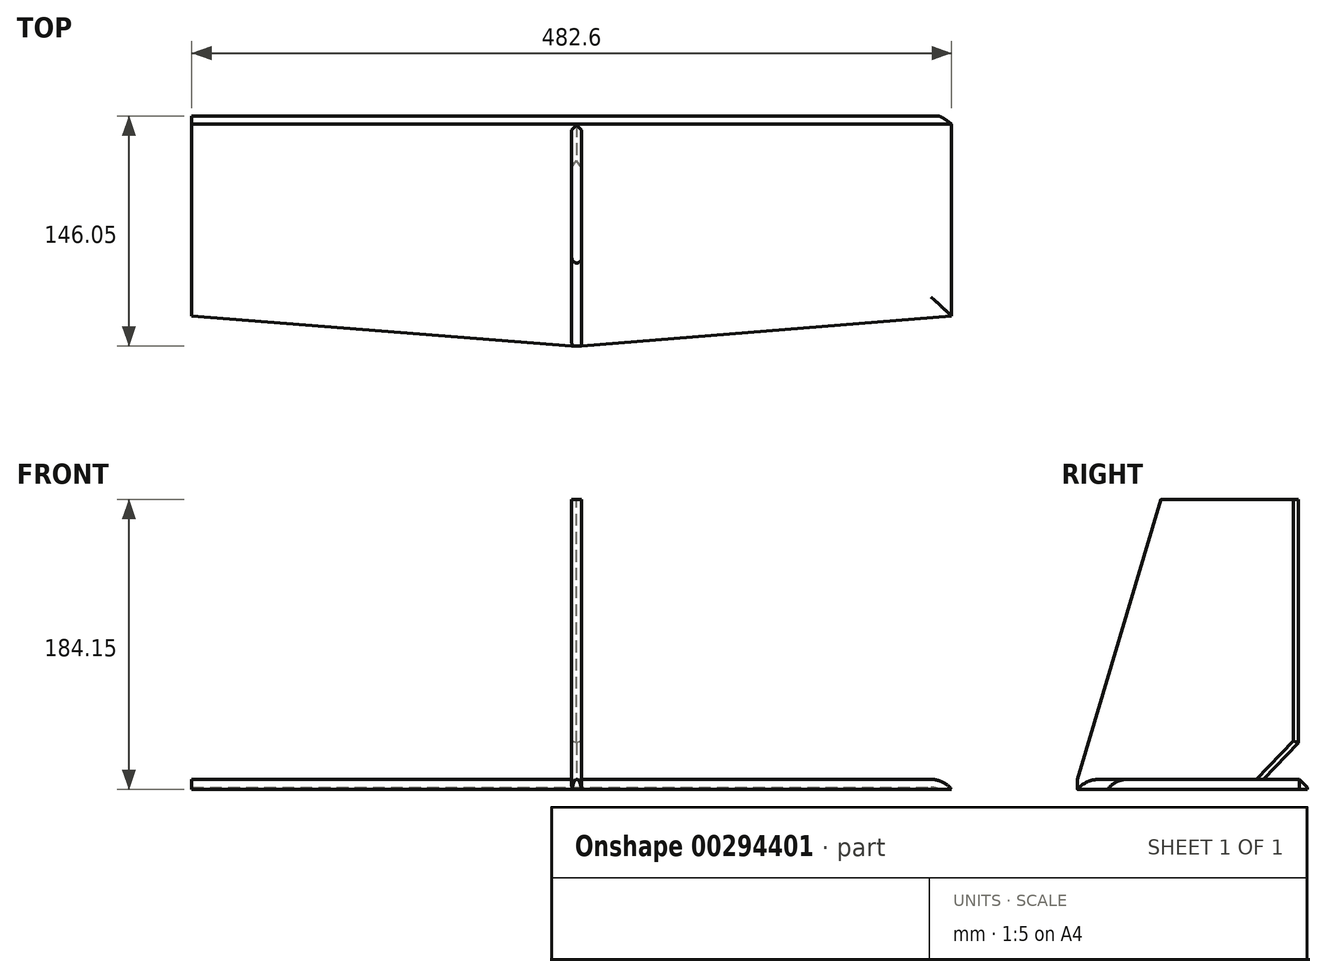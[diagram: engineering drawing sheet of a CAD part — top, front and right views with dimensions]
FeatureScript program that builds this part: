
annotation { "Feature Type Name" : "Feature", "Feature Type Description" : "" }
export const myFeature = defineFeature(function(context is Context, id is Id, definition is map)
    precondition{}
    {
        {
            var Q0;
            Q0=qCreatedBy(makeId("Right.planeOp"),FACE);
            var sketch = newSketch(context, id + "F0", { "sketchPlane" : qUnion([Q0])});
            skLineSegment(sketch, "E0.bottom", {"start": v(0, 85.16) * mm, "end": v(89.45, 85.16) * mm});
            skLineSegment(sketch, "E0.top", {"start": v(-52.8, -92.64) * mm, "end": v(67.7, -92.64) * mm});
            skLineSegment(sketch, "E0.right", {"start": v(89.45, 85.16) * mm, "end": v(89.45, -70.22) * mm});
            skLineSegment(sketch, "E1", {"start": v(-52.8, -92.64) * mm, "end": v(0, 85.16) * mm});
            skLineSegment(sketch, "E2", {"start": v(89.45, -70.22) * mm, "end": v(67.7, -92.64) * mm});
            skSolve(sketch);
        }
        {
            var Q0;
            Q0=makeQuery(id+"F0.imprint","IMPRINT",FACE,{"disambiguationData":[TD([[makeQuery(id+"F0.imprint","IMPRINT",EDGE,{"derivedFrom":sQuery(id+"F0.wireOp",EDGE,"E0.bottom")}),-1.0]])]});
            extrude(context, id + "F1", {"entities" : qUnion([Q0]), "depth" : 6.35 * mm, "offsetDistance" : 25.4 * mm});
        }
        {
            var Q0;
            Q0=makeQuery(id+"F1.opExtrude","SWEPT_FACE",FACE,{"disambiguationData":[OSD([sQuery(id+"F0.wireOp",EDGE,"E0.top")])]});
            var sketch = newSketch(context, id + "F2", { "sketchPlane" : qUnion([Q0])});
            skLineSegment(sketch, "E3.bottom", {"start": v(0, 52.8) * mm, "end": v(6.35, 52.8) * mm});
            skLineSegment(sketch, "E3.top", {"start": v(-241.3, -93.26) * mm, "end": v(241.3, -93.26) * mm});
            skLineSegment(sketch, "E3.left", {"start": v(-241.3, 33.74) * mm, "end": v(-241.3, -93.26) * mm});
            skLineSegment(sketch, "E3.right", {"start": v(241.3, 33.74) * mm, "end": v(241.3, -93.26) * mm});
            skLineSegment(sketch, "E4", {"start": v(0, 52.8) * mm, "end": v(-241.3, 33.74) * mm});
            skLineSegment(sketch, "E5", {"start": v(6.35, 52.8) * mm, "end": v(241.3, 33.74) * mm});
            skPoint(sketch, "E6.orphan", {"position": v(-241.3, 52.8) * mm});
            skPoint(sketch, "E7.center.orphan", {"position": v(241.37, 14.7) * mm});
            skPoint(sketch, "E8.center.orphan", {"position": v(-222.25, 14.7) * mm});
            skSolve(sketch);
        }
        {
            var Q0;
            Q0 = qSketchRegion(id + "F2", true);
            extrude(context, id + "F3", {"entities" : qUnion([Q0]), "operationType" : NewBodyOperationType.ADD, "depth" : 6.35 * mm, "offsetDistance" : 25.4 * mm});
        }
        {
            var Q0;
            Q0=makeQuery(id+"F1.opExtrude","CAP_EDGE",EDGE,{"disambiguationData":[OSD([sQuery(id+"F0.wireOp",EDGE,"E1")])],"isStart":false});
            var Q1;
            Q1=makeQuery(id+"F1.opExtrude","CAP_EDGE",EDGE,{"disambiguationData":[OSD([sQuery(id+"F0.wireOp",EDGE,"E1")])],"isStart":true});
            fillet(context, id + "F4", {"entities" : qUnion([Q0, Q1]), "radius" : 3.07 * mm, "tangentPropagation" : true, "allowEdgeOverflow" : false});
        }
        {
            var Q0;
            Q0=makeQuery(id+"F3.opExtrude","CAP_EDGE",EDGE,{"disambiguationData":[OSD([sQuery(id+"F2.wireOp",EDGE,"E5")])],"isStart":true});
            var Q1;
            Q1=makeQuery(id+"F3.opExtrude","CAP_EDGE",EDGE,{"disambiguationData":[OSD([sQuery(id+"F2.wireOp",EDGE,"E4")])],"isStart":true});
            var Q2;
            Q2=makeQuery(id+"F3.opExtrude","CAP_EDGE",EDGE,{"disambiguationData":[OSD([sQuery(id+"F2.wireOp",EDGE,"E7")])],"isStart":true});
            var Q3;
            Q3=makeQuery(id+"F3.opExtrude","CAP_EDGE",EDGE,{"disambiguationData":[OSD([sQuery(id+"F2.wireOp",EDGE,"E3.right")])],"isStart":true});
            fillet(context, id + "F5", {"entities" : qUnion([Q0, Q1, Q2, Q3]), "radius" : 16.56 * mm, "tangentPropagation" : true, "allowEdgeOverflow" : false});
        }
        {
            var Q0;
            Q0=makeQuery(id+"F1.opExtrude","CAP_EDGE",EDGE,{"disambiguationData":[OSD([sQuery(id+"F0.wireOp",EDGE,"E0.right")])],"isStart":true});
            var Q1;
            Q1=makeQuery(id+"F1.opExtrude","CAP_EDGE",EDGE,{"disambiguationData":[OSD([sQuery(id+"F0.wireOp",EDGE,"E0.right")])],"isStart":false});
            chamfer(context, id + "F6", {"entities" : qUnion([Q0, Q1]), "width" : 5.08 * mm, "tangentPropagation" : true});
        }
        {
            var Q0;
            Q0=makeQuery(id+"F1.opExtrude","CAP_EDGE",EDGE,{"disambiguationData":[OSD([sQuery(id+"F0.wireOp",EDGE,"E2")])],"isStart":false});
            var Q1;
            Q1=makeQuery(id+"F1.opExtrude","CAP_EDGE",EDGE,{"disambiguationData":[OSD([sQuery(id+"F0.wireOp",EDGE,"E2")])],"isStart":true});
            chamfer(context, id + "F7", {"entities" : qUnion([Q0, Q1]), "width" : 5.08 * mm, "tangentPropagation" : true});
        }
        {
            var Q0;
            Q0=makeQuery(id+"F3.opExtrude","CAP_EDGE",EDGE,{"disambiguationData":[OSD([sQuery(id+"F2.wireOp",EDGE,"E3.top")])],"isStart":true});
            chamfer(context, id + "F8", {"entities" : qUnion([Q0]), "width" : 5.08 * mm, "tangentPropagation" : true});
        }
    });
